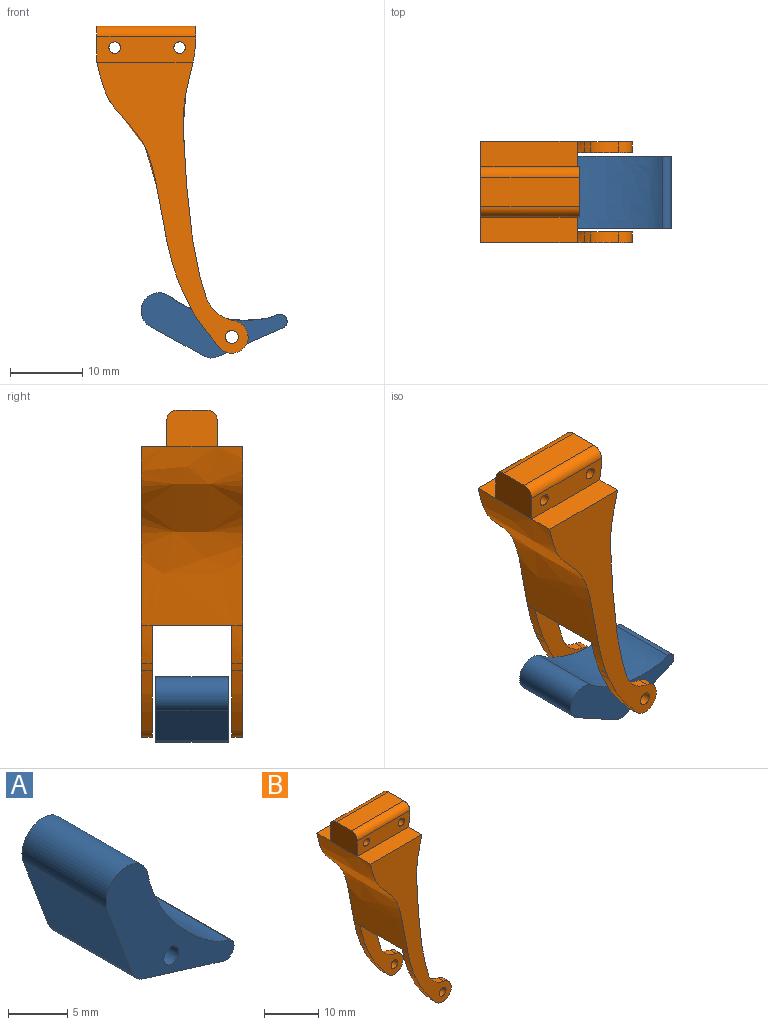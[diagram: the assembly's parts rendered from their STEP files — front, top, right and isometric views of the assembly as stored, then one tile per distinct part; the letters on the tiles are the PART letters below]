
ASSEMBLY  parts=2 mates=1
PART A: 9 faces, bbox 18.1x13.8x18.4 mm
  f0: plane 10x7.98mm, normal (-0.94,0,-0.35), area 85.2mm2, adj f1,f4,f6,f7
  f1: cylinder r=2mm len=10mm, axis (0,1,0), area 18.3mm2, adj f0,f2,f6,f7
  f2: plane 10x9.51mm, normal (-0.29,0,-0.96), area 99.5mm2, adj f1,f3,f6,f7
  f3: cylinder r=1mm len=10mm, axis (0,1,0), area 29.4mm2, adj f2,f6,f7,f8
  f4: cylinder r=2.5mm len=10mm, axis (0,1,0), area 79.9mm2, adj f0,f6,f7,f8
  f5: cylinder r=0.9mm len=10mm, axis (0,1,0), area 56.5mm2, adj f6,f7
  f6: plane 18.37x18.06mm, normal (0,-1,0), area 83.4mm2, adj f0,f1,f2,f3,f4,f5,f8
  f7: plane 18.34x18.03mm, normal (0,1,0), area 83.3mm2, adj f0,f1,f2,f3,f4,f5,f8
  f8: bspline ~11.97x11mm, area 160.8mm2, adj f3,f4,f6,f7
PART B: 33 faces, bbox 21.2x14x45.3 mm
  f0: plane 13.63x4mm, normal (0,0,1), area 54.5mm2, adj f3,f4,f5,f30
  f1: extruded ~24.8x14mm, area 380.6mm2, adj f9,f14,f18,f23,f24,f28,f29,f30
  f2: plane 13.72x3.54mm, normal (0,-1,0), area 43.5mm2, adj f4,f5,f29,f30,f31,f32
  f3: cylinder r=1.5mm len=13.7mm, axis (1,0,0), area 32.2mm2, adj f0,f5,f27,f30
  f4: cylinder r=1.5mm len=13.7mm, axis (-1,0,0), area 32.2mm2, adj f0,f2,f5,f30
  f5: extruded ~29.53x14mm, area 380.3mm2, adj f0,f2,f3,f4,f7,f14,f16,f23
  f6: plane 16.18x11.25mm, normal (0,-1,0), area 56.2mm2, adj f7,f8,f9,f10,f11,f12,f13,f24
  f7: extruded ~5.45x1.5mm, area 8.3mm2, adj f5,f6,f13,f14
  f8: cylinder r=0.9mm len=1.8mm, axis (0,-1,0), area 8.5mm2, adj f6,f14
  f9: extruded ~5.29x1.5mm, area 8.2mm2, adj f1,f6,f10,f14
  f10: extruded ~1.5x1.07mm, area 1.7mm2, adj f6,f9,f11,f14
  f11: extruded ~8.36x5.35mm, area 15mm2, adj f6,f10,f12,f14
  f12: cylinder r=2.25mm len=4.47mm, axis (0,-1,0), area 13mm2, adj f6,f11,f14,f26
  f13: extruded ~2.65x1.5mm, area 4.2mm2, adj f6,f7,f14,f26
  f14: plane 40.55x21.16mm, normal (0,1,0), area 222.3mm2, adj f1,f5,f7,f8,f9,f10,f11,f12
  f15: plane 16.18x11.25mm, normal (0,1,0), area 56.2mm2, adj f16,f17,f18,f19,f20,f21,f22,f24
  f16: extruded ~5.45x1.5mm, area 8.3mm2, adj f5,f15,f22,f23
  f17: cylinder r=0.9mm len=1.8mm, axis (0,-1,0), area 8.5mm2, adj f15,f23
  f18: extruded ~5.29x1.5mm, area 8.2mm2, adj f1,f15,f19,f23
  f19: extruded ~1.5x1.07mm, area 1.7mm2, adj f15,f18,f20,f23
  f20: extruded ~8.36x5.35mm, area 15mm2, adj f15,f19,f21,f23
  f21: cylinder r=2.25mm len=4.47mm, axis (0,-1,0), area 13mm2, adj f15,f20,f23,f25
  f22: extruded ~2.65x1.5mm, area 4.2mm2, adj f15,f16,f23,f25
  f23: plane 40.55x21.16mm, normal (0,-1,0), area 222.3mm2, adj f1,f5,f16,f17,f18,f19,f20,f21
  f24: cylinder r=3.5mm len=11mm, axis (0,1,0), area 41.1mm2, adj f1,f5,f6,f15
  f25: cylinder r=5mm len=3.91mm, axis (0,-1,0), area 8mm2, adj f15,f21,f22,f23
  f26: cylinder r=5mm len=3.91mm, axis (0,-1,0), area 8mm2, adj f6,f12,f13,f14
  f27: plane 13.72x3.54mm, normal (0,1,0), area 43.5mm2, adj f3,f5,f28,f30,f31,f32
  f28: plane 13.32x3.5mm, normal (0,0,1), area 46.6mm2, adj f1,f5,f14,f27
  f29: plane 13.32x3.5mm, normal (0,0,1), area 46.6mm2, adj f1,f2,f5,f23
  f30: plane 7x5mm, normal (-1,0,0), area 34mm2, adj f0,f1,f2,f3,f4,f27
  f31: cylinder r=0.8mm len=7mm, axis (0,1,0), area 35.2mm2, adj f2,f27
  f32: cylinder r=0.8mm len=7mm, axis (0,1,0), area 35.2mm2, adj f2,f27
PLACE A rot(axis=(0,-1,0),40.8deg) t=(-0.13,5,-10.03)mm
PLACE B t=(-1.52,5,-0.02)mm fixed
MATE revolute A.f5 <-> B.f8  axis (0,-1,0) through (-0.13,-5,-10.03)mm
